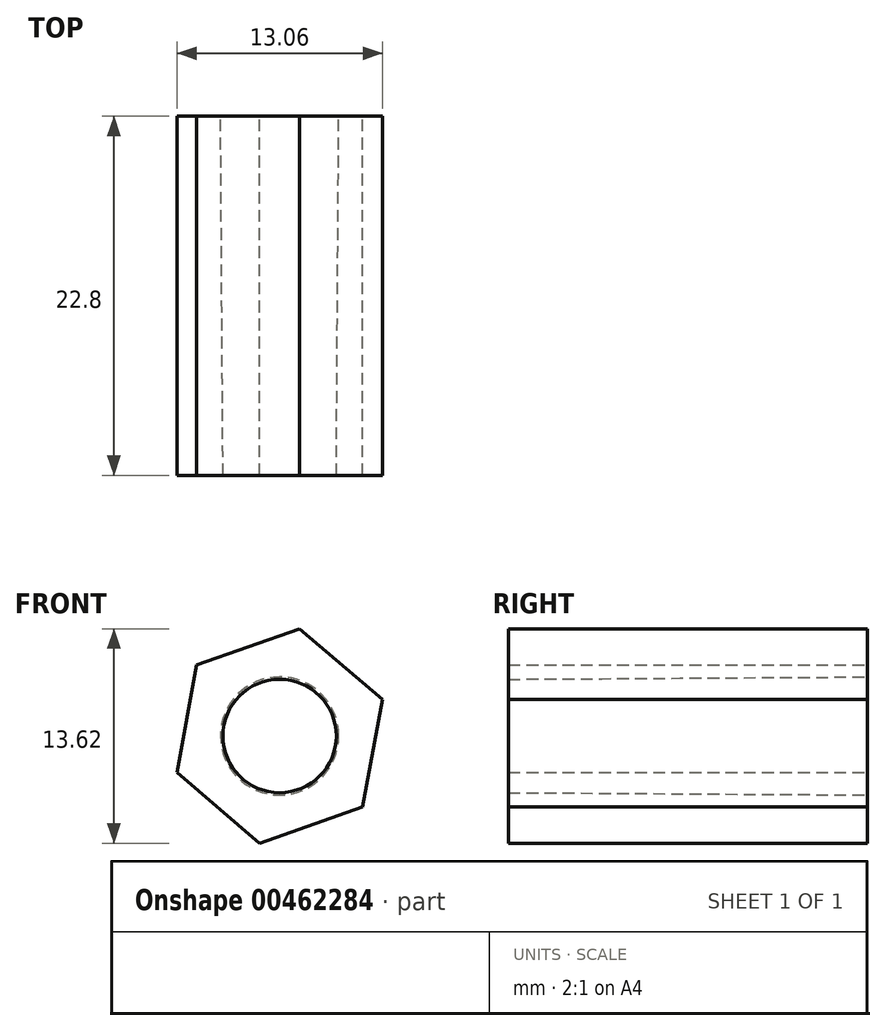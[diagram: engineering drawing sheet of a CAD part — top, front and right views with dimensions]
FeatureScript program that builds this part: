
annotation { "Feature Type Name" : "Feature", "Feature Type Description" : "" }
export const myFeature = defineFeature(function(context is Context, id is Id, definition is map)
    precondition{}
    {
        {
            var Q0;
            Q0=qCreatedBy(makeId("Front.planeOp"),FACE);
            var sketch = newSketch(context, id + "F0", { "sketchPlane" : qUnion([Q0])});
            skCircle(sketch, "E0.cCircle", {"center": v(0, 0) * mm, "radius": 6.93 * mm, "construction": true});
            skLineSegment(sketch, "E0.0", {"start": v(5.27, -4.5) * mm, "end": v(-1.26, -6.81) * mm});
            skLineSegment(sketch, "E0.1", {"start": v(-1.26, -6.81) * mm, "end": v(-6.53, -2.31) * mm});
            skLineSegment(sketch, "E0.2", {"start": v(-6.53, -2.31) * mm, "end": v(-5.27, 4.5) * mm});
            skLineSegment(sketch, "E0.3", {"start": v(-5.27, 4.5) * mm, "end": v(1.26, 6.81) * mm});
            skLineSegment(sketch, "E0.4", {"start": v(1.26, 6.81) * mm, "end": v(6.53, 2.31) * mm});
            skLineSegment(sketch, "E0.5", {"start": v(6.53, 2.31) * mm, "end": v(5.27, -4.5) * mm});
            skSolve(sketch);
        }
        {
            var Q0;
            Q0=makeQuery(id+"F0.imprint","IMPRINT",FACE,{"disambiguationData":[TD([[makeQuery(id+"F0.imprint","IMPRINT",EDGE,{"derivedFrom":sQuery(id+"F0.wireOp",EDGE,"E0.0")}),-1.0]])]});
            extrude(context, id + "F1", {"entities" : qUnion([Q0]), "endBound" : BoundingType.SYMMETRIC, "depth" : 22.8 * mm});
        }
        {
            var Q0;
            Q0=makeQuery(id+"F1.opExtrude","CAP_FACE",FACE,{"disambiguationData":[OSD([sQuery(id+"F0.wireOp",EDGE,"E0.0"),sQuery(id+"F0.wireOp",EDGE,"E0.1"),sQuery(id+"F0.wireOp",EDGE,"E0.2"),sQuery(id+"F0.wireOp",EDGE,"E0.3"),sQuery(id+"F0.wireOp",EDGE,"E0.4"),sQuery(id+"F0.wireOp",EDGE,"E0.5")])],"isStart":true});
            var sketch = newSketch(context, id + "F2", { "sketchPlane" : qUnion([Q0])});
            skCircle(sketch, "E1", {"center": v(0, 0) * mm, "radius": 3.75 * mm});
            skSolve(sketch);
        }
        {
            var Q0;
            Q0=makeQuery(id+"F1.opExtrude","CAP_FACE",FACE,{"disambiguationData":[OSD([sQuery(id+"F0.wireOp",EDGE,"E0.0"),sQuery(id+"F0.wireOp",EDGE,"E0.1"),sQuery(id+"F0.wireOp",EDGE,"E0.2"),sQuery(id+"F0.wireOp",EDGE,"E0.3"),sQuery(id+"F0.wireOp",EDGE,"E0.4"),sQuery(id+"F0.wireOp",EDGE,"E0.5")])],"isStart":false});
            var sketch = newSketch(context, id + "F3", { "sketchPlane" : qUnion([Q0])});
            skCircle(sketch, "E2", {"center": v(0, 0) * mm, "radius": 3.6 * mm});
            skSolve(sketch);
        }
        {
            var Q1;
            Q1=makeQuery(id+"F3.imprint","IMPRINT",FACE,{"disambiguationData":[TD([[makeQuery(id+"F3.imprint","IMPRINT",EDGE,{"derivedFrom":sQuery(id+"F3.wireOp",EDGE,"E2")}),1.0]])]});
            var Q2;
            Q2=makeQuery(id+"F2.imprint","IMPRINT",FACE,{"disambiguationData":[TD([[makeQuery(id+"F2.imprint","IMPRINT",EDGE,{"derivedFrom":sQuery(id+"F2.wireOp",EDGE,"E1")}),1.0]])]});
            loft(context, id + "F4", {"operationType" : NewBodyOperationType.REMOVE, "sheetProfilesArray" : [{ "sheetProfileEntities" : qUnion([Q1]) }, { "sheetProfileEntities" : qUnion([Q2]) }]});
        }
    });
